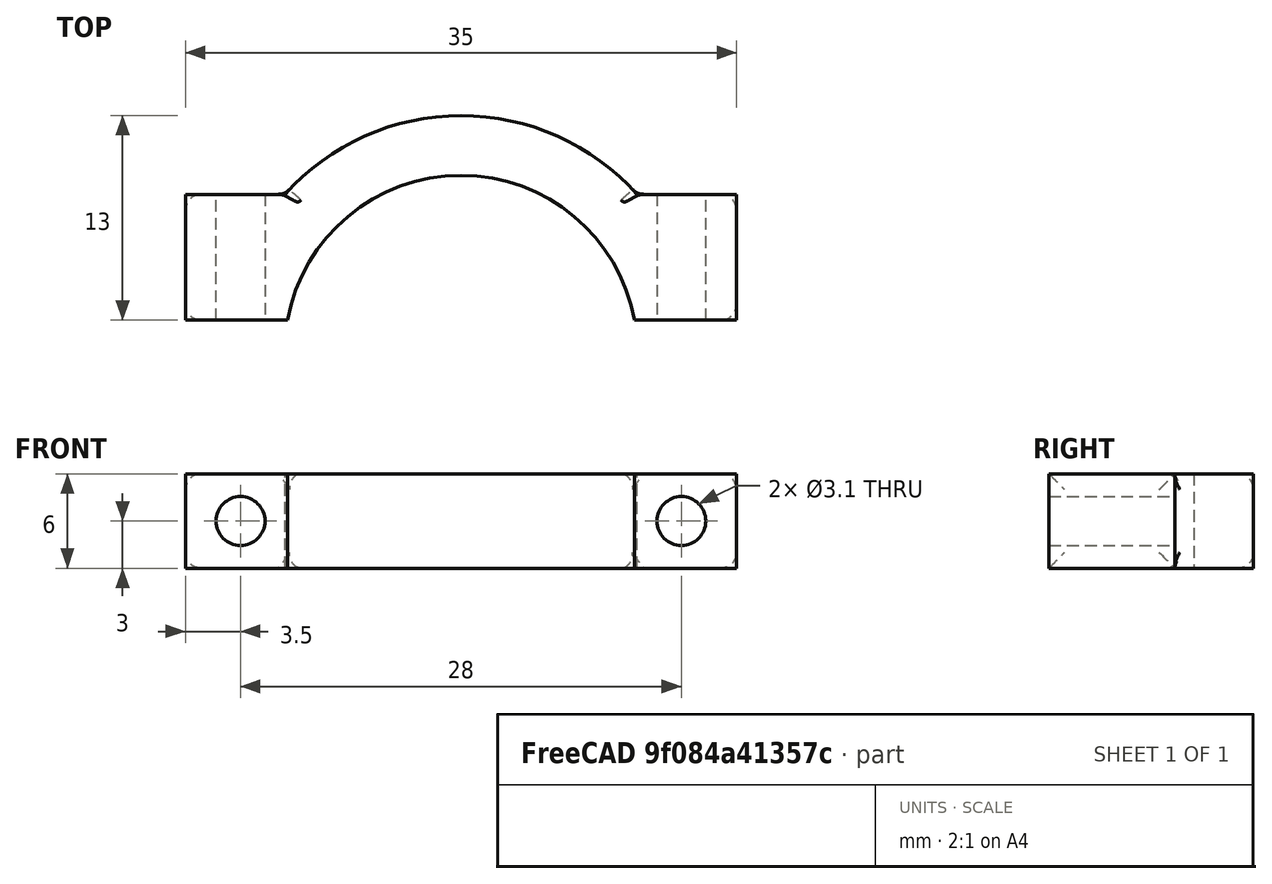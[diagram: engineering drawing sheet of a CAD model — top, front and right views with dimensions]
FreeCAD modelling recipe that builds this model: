
FCSTD DOCUMENT  (FreeCAD 0.16R)
Label: Caps
License: All rights reserved
LicenseURL: http://en.wikipedia.org/wiki/All_rights_reserved
objects: PartDesign::Fillet×3, Sketcher::SketchObject×2, PartDesign::Pad×1, PartDesign::Pocket×1, PartDesign::Mirrored×1, Mesh::Feature×1
note: 10 computed .brp shape members not serialized (recipe doc carries the construction recipe); baked Part::Feature solids carry a one-line shape summary decoded from their .brp

FEATURE [Sketcher::SketchObject] Sketch
  sketch-geometry (8):
    g0: ArcOfCircle CenterX=0 CenterY=0 CenterZ=0 NormalX=0 NormalY=0 NormalZ=1 Radius=11.2 StartAngle=0.179534 EndAngle=2.96206
    g1: ArcOfCircle CenterX=0 CenterY=0 CenterZ=0 NormalX=0 NormalY=0 NormalZ=1 Radius=15 StartAngle=0.729728 EndAngle=2.41186
    g2: LineSegment StartX=-17.5 StartY=10 StartZ=0 EndX=-11.1803 EndY=10 EndZ=0
    g3: LineSegment StartX=17.5 StartY=10 StartZ=0 EndX=17.5 EndY=2 EndZ=0
    g4: LineSegment StartX=17.5 StartY=2 StartZ=0 EndX=11.02 EndY=2 EndZ=0
    g5: LineSegment StartX=-17.5 StartY=2 StartZ=0 EndX=-17.5 EndY=10 EndZ=0
    g6: LineSegment StartX=11.1803 StartY=10 StartZ=0 EndX=17.5 EndY=10 EndZ=0
    g7: LineSegment StartX=-11.02 StartY=2 StartZ=0 EndX=-17.5 EndY=2 EndZ=0
  constraints (22):
    c: Radius(g1) = 15
    c: Radius(g0) = 11.2
    c: Coincident(g0,g-1)
    c: Coincident(g1,g-1)
    c: Coincident(g6,g3)
    c: Coincident(g3,g4)
    c: Coincident(g7,g5)
    c: Coincident(g5,g2)
    c: Horizontal(g2)
    c: Horizontal(g4)
    c: Vertical(g3)
    c: Vertical(g5)
    c: DistanceX(g2,g6) = 35
    c: DistanceY(g3,g3) = 8
    c: Symmetric(g6,g2,g-2)
    c: DistanceY(g7,g-1) = -2
    c: Tangent(g2,g6)
    c: Coincident(g4,g0)
    c: Coincident(g7,g0)
    c: Tangent(g4,g7)
    c: Coincident(g2,g1)
    c: Coincident(g6,g1)
FEATURE [PartDesign::Pad] Pad
  Length = 6
  Length2 = 100
  Sketch = -> Sketch
  Type = 0
FEATURE [Sketcher::SketchObject] Sketch001
  Placement = pos=(0,10,0) rot=(0,0.707107,0.707107;3.14159rad)
  Support = -> Pad [Face7]
  sketch-geometry (1):
    g0: Circle CenterX=-14 CenterY=3 CenterZ=0 NormalX=0 NormalY=0 NormalZ=1 Radius=1.55
  constraints (3):
    c: DistanceY(g-1,g0) = 3
    c: Radius(g0) = 1.55
    c: DistanceX(g0,g-1) = 14
FEATURE [PartDesign::Pocket] Pocket
  Length = 5
  Sketch = -> Sketch001
  Type = 1
FEATURE [PartDesign::Mirrored] Mirrored
  MirrorPlane = -> Sketch001 [V_Axis]
  Originals = -> [Pocket]
FEATURE [PartDesign::Fillet] Fillet
  Base = -> Mirrored [Edge28,Edge24,Edge13,Edge19]
  Radius = 1
FEATURE [PartDesign::Fillet] Fillet001
  Base = -> Fillet [Edge27,Edge22,Edge7,Edge28]
  Radius = 1
FEATURE [PartDesign::Fillet] Fillet002
  Base = -> Fillet001 [Edge19,Edge25,Edge6,Edge26]
  Radius = 1
FEATURE [Mesh::Feature] Mesh  label="Fillet002 (Meshed)"
